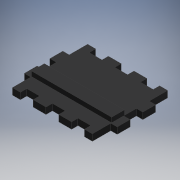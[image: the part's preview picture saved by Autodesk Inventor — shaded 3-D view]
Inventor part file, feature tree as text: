
AUTODESK INVENTOR PART (.ipt)
format: ipt  version: 2019 (Build 230136000, 136)  size: 186,880 bytes
history: native  units: mm
features: extrude x3, sketch x3
ambient origin geometry x8: Origin, YZ Plane, XZ Plane, XY Plane, X Axis, Y Axis, Z Axis, Center Point
bodies: Solid1 (feature_tree)
feature tree (6):
  extrude  "Extrusion1"  Depth=47.0mm
  extrude  "Extrusion2"  Depth=4.0mm
  extrude  "Extrusion3"  Depth=8.0mm
  sketch  "Sketch1"  dims[d0=58.0mm d1=47.0mm]
  sketch  "Sketch2"  dims[d6=4.0mm d7=0.0mm d8=4.0mm]
  sketch  "Sketch3"  dims[d11=8.0mm d12=8.0mm d13=4.0mm d14=4.0mm d15=0.0mm d16=4.0mm d17=8.0mm d18=8.0mm d19=8.0mm d20=3.0mm d21=0.0mm]
